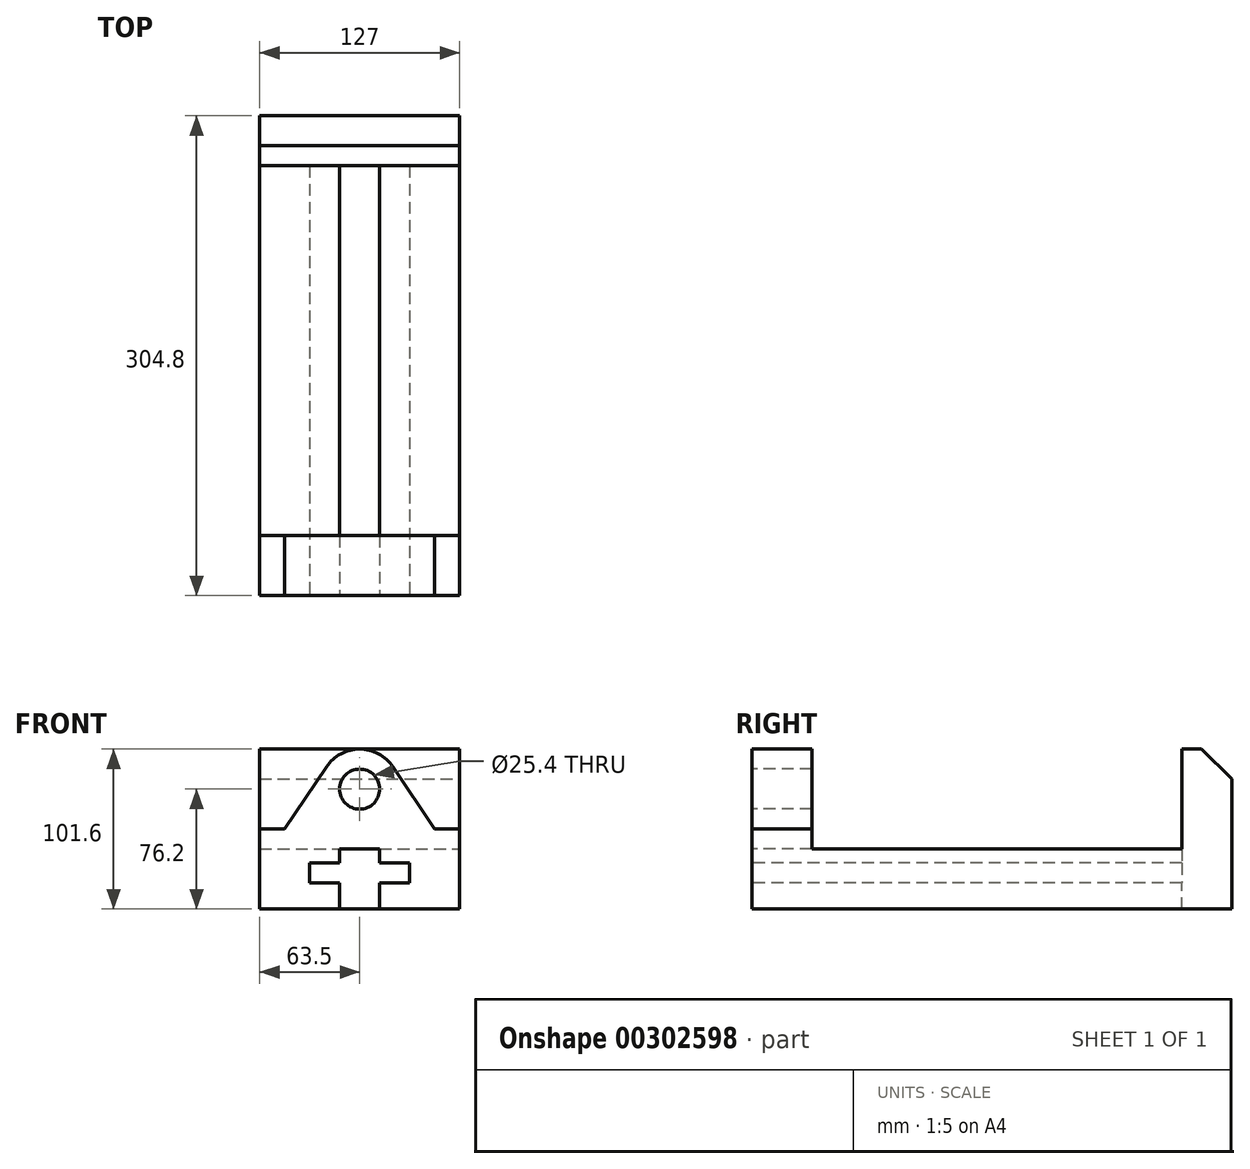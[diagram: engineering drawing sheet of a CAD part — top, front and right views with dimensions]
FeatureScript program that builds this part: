
annotation { "Feature Type Name" : "Feature", "Feature Type Description" : "" }
export const myFeature = defineFeature(function(context is Context, id is Id, definition is map)
    precondition{}
    {
        {
            var Q0;
            Q0=qCreatedBy(makeId("Front.planeOp"),FACE);
            var sketch = newSketch(context, id + "F0", { "sketchPlane" : qUnion([Q0])});
            skLineSegment(sketch, "E0.bottom", {"start": v(0, 0) * mm, "end": v(127, 0) * mm});
            skLineSegment(sketch, "E0.top", {"start": v(0, 101.6) * mm, "end": v(127, 101.6) * mm});
            skLineSegment(sketch, "E0.left", {"start": v(0, 0) * mm, "end": v(0, 101.6) * mm});
            skLineSegment(sketch, "E0.right", {"start": v(127, 0) * mm, "end": v(127, 101.6) * mm});
            skSolve(sketch);
        }
        {
            var Q0;
            Q0=makeQuery(id+"F0.imprint","IMPRINT",FACE,{"disambiguationData":[TD([[makeQuery(id+"F0.imprint","IMPRINT",EDGE,{"derivedFrom":sQuery(id+"F0.wireOp",EDGE,"E0.bottom")}),1.0]])]});
            extrude(context, id + "F1", {"entities" : qUnion([Q0]), "depth" : 304.8 * mm});
        }
        {
            var Q0;
            Q0=makeQuery(id+"F1.opExtrude","CAP_FACE",FACE,{"disambiguationData":[OSD([sQuery(id+"F0.wireOp",EDGE,"E0.bottom"),sQuery(id+"F0.wireOp",EDGE,"E0.top"),sQuery(id+"F0.wireOp",EDGE,"E0.left"),sQuery(id+"F0.wireOp",EDGE,"E0.right")])],"isStart":false});
            var sketch = newSketch(context, id + "F2", { "sketchPlane" : qUnion([Q0])});
            skLineSegment(sketch, "E1", {"start": v(50.8, 0) * mm, "end": v(50.8, 16.51) * mm});
            skLineSegment(sketch, "E2", {"start": v(50.8, 16.51) * mm, "end": v(31.75, 16.51) * mm});
            skLineSegment(sketch, "E3", {"start": v(31.75, 16.51) * mm, "end": v(31.75, 29.21) * mm});
            skLineSegment(sketch, "E4", {"start": v(31.75, 29.21) * mm, "end": v(50.8, 29.21) * mm});
            skLineSegment(sketch, "E5", {"start": v(50.8, 29.21) * mm, "end": v(50.8, 38.1) * mm});
            skLineSegment(sketch, "E6", {"start": v(50.8, 38.1) * mm, "end": v(76.2, 38.1) * mm});
            skLineSegment(sketch, "E7", {"start": v(76.2, 38.1) * mm, "end": v(76.2, 29.21) * mm});
            skLineSegment(sketch, "E8", {"start": v(76.2, 29.2) * mm, "end": v(95.25, 29.21) * mm});
            skLineSegment(sketch, "E9", {"start": v(95.25, 29.21) * mm, "end": v(95.25, 16.51) * mm});
            skLineSegment(sketch, "E10", {"start": v(95.25, 16.51) * mm, "end": v(76.2, 16.51) * mm});
            skLineSegment(sketch, "E11", {"start": v(76.2, 16.51) * mm, "end": v(76.2, 0) * mm});
            skLineSegment(sketch, "E12", {"start": v(76.2, 0) * mm, "end": v(50.8, 0) * mm});
            skLineSegment(sketch, "E13", {"start": v(63.5, 0) * mm, "end": v(63.5, 105.38) * mm, "construction": true});
            skSolve(sketch);
        }
        {
            var Q0;
            Q0=makeQuery(id+"F2.imprint","IMPRINT",FACE,{"disambiguationData":[TD([[makeQuery(id+"F2.imprint","IMPRINT",EDGE,{"derivedFrom":sQuery(id+"F2.wireOp",EDGE,"E1")}),-1.0]])]});
            extrude(context, id + "F3", {"entities" : qUnion([Q0]), "operationType" : NewBodyOperationType.REMOVE, "oppositeDirection" : true, "depth" : 273.05 * mm});
        }
        {
            var Q0;
            Q0=makeQuery(id+"F1.opExtrude","CAP_FACE",FACE,{"disambiguationData":[OSD([sQuery(id+"F0.wireOp",EDGE,"E0.bottom"),sQuery(id+"F0.wireOp",EDGE,"E0.top"),sQuery(id+"F0.wireOp",EDGE,"E0.left"),sQuery(id+"F0.wireOp",EDGE,"E0.right")])],"isStart":false});
            var sketch = newSketch(context, id + "F4", { "sketchPlane" : qUnion([Q0])});
            skLineSegment(sketch, "E14", {"start": v(0, 50.8) * mm, "end": v(15.88, 50.8) * mm});
            skLineSegment(sketch, "E15", {"start": v(15.87, 50.8) * mm, "end": v(42.4, 90.35) * mm});
            skLineSegment(sketch, "E16", {"start": v(127, 50.8) * mm, "end": v(111.13, 50.8) * mm});
            skPoint(sketch, "E16.startSnap0", {"position": v(127, 50.8) * mm});
            skLineSegment(sketch, "E17", {"start": v(111.13, 50.8) * mm, "end": v(84.6, 90.35) * mm});
            skArc(sketch, "E18", {"start": v(42.4, 90.35) * mm, "mid": v(63.5, 101.6) * mm, "end": v(84.6, 90.35) * mm});
            skLineSegment(sketch, "E19.0", {"start": v(0, 101.6) * mm, "end": v(127, 101.6) * mm});
            skPoint(sketch, "E20.startSnap0", {"position": v(63.5, 101.6) * mm});
            skCircle(sketch, "E21", {"center": v(63.5, 76.2) * mm, "radius": 12.7 * mm});
            skSolve(sketch);
        }
        {
            var Q0;
            {var subQ6=sQuery(id+"F4.wireOp",EDGE,"E14");Q0=makeQuery(id+"F4.imprint","IMPRINT",FACE,{"disambiguationData":[TD([[makeQuery(id+"F4.imprint","IMPRINT",EDGE,{"derivedFrom":subQ6}),1.0]])]});}
            var Q1;
            {var subQ6=sQuery(id+"F4.wireOp",EDGE,"E16");Q1=makeQuery(id+"F4.imprint","IMPRINT",FACE,{"disambiguationData":[TD([[makeQuery(id+"F4.imprint","IMPRINT",EDGE,{"derivedFrom":subQ6}),-1.0]])]});}
            extrude(context, id + "F5", {"entities" : qUnion([Q0, Q1]), "operationType" : NewBodyOperationType.REMOVE, "oppositeDirection" : true, "depth" : 273.05 * mm});
        }
        {
            var Q0;
            Q0=makeQuery(id+"F1.opExtrude","SWEPT_FACE",FACE,{"disambiguationData":[OSD([sQuery(id+"F0.wireOp",EDGE,"E0.top")])]});
            var sketch = newSketch(context, id + "F6", { "sketchPlane" : qUnion([Q0])});
            skLineSegment(sketch, "E22.bottom", {"start": v(127, -31.75) * mm, "end": v(0, -31.75) * mm});
            skLineSegment(sketch, "E22.top", {"start": v(127, -266.7) * mm, "end": v(0, -266.7) * mm});
            skLineSegment(sketch, "E22.left", {"start": v(127, -31.75) * mm, "end": v(127, -266.7) * mm});
            skLineSegment(sketch, "E22.right", {"start": v(0, -31.75) * mm, "end": v(0, -266.7) * mm});
            skSolve(sketch);
        }
        {
            var Q0;
            Q0=makeQuery(id+"F6.imprint","IMPRINT",FACE,{"disambiguationData":[TD([[makeQuery(id+"F6.imprint","IMPRINT",EDGE,{"derivedFrom":sQuery(id+"F6.wireOp",EDGE,"E22.top")}),-1.0]])]});
            extrude(context, id + "F7", {"entities" : qUnion([Q0]), "operationType" : NewBodyOperationType.REMOVE, "oppositeDirection" : true, "depth" : 63.5 * mm});
        }
        {
            var Q0;
            Q0=makeQuery(id+"F4.imprint","IMPRINT",FACE,{"disambiguationData":[TD([[makeQuery(id+"F4.imprint","IMPRINT",EDGE,{"derivedFrom":sQuery(id+"F4.wireOp",EDGE,"E21")}),1.0]])]});
            extrude(context, id + "F8", {"entities" : qUnion([Q0]), "operationType" : NewBodyOperationType.REMOVE, "oppositeDirection" : true, "depth" : 38.1 * mm});
        }
        {
            var Q0;
            Q0=makeQuery(id+"F1.opExtrude","CAP_EDGE",EDGE,{"disambiguationData":[OSD([sQuery(id+"F0.wireOp",EDGE,"E0.top")])],"isStart":true});
            chamfer(context, id + "F9", {"entities" : qUnion([Q0]), "chamferType" : ChamferType.TWO_OFFSETS, "width1" : 19.05 * mm, "oppositeDirection" : false, "width2" : 19.05 * mm, "tangentPropagation" : true});
        }
    });
